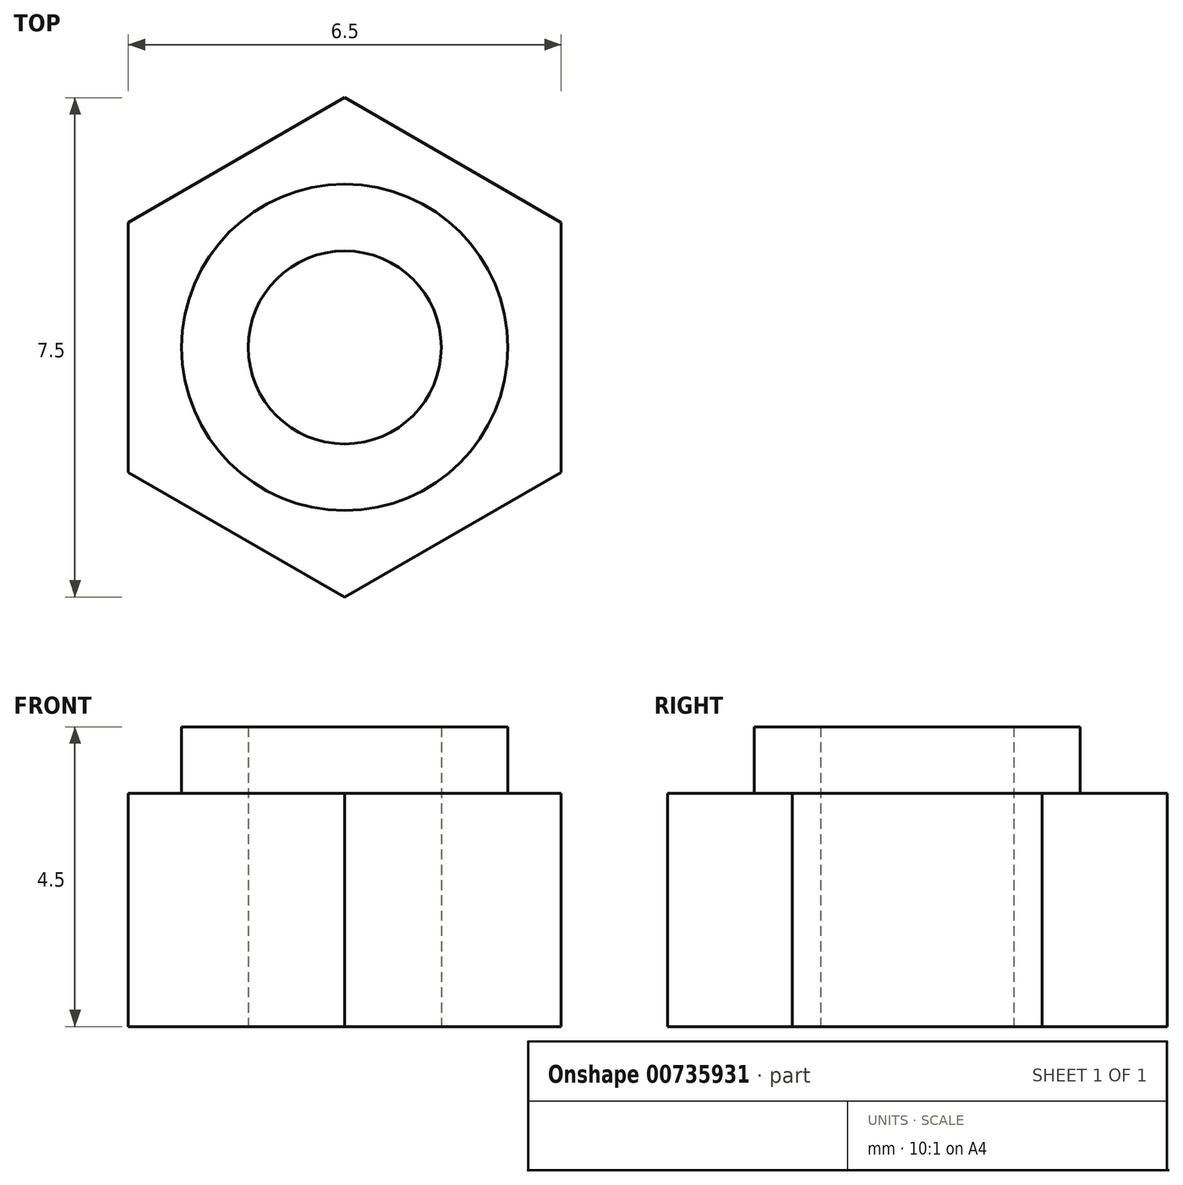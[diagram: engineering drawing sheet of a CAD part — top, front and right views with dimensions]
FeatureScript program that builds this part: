
annotation { "Feature Type Name" : "Feature", "Feature Type Description" : "" }
export const myFeature = defineFeature(function(context is Context, id is Id, definition is map)
    precondition{}
    {
        {
            var Q0;
            Q0=qCreatedBy(makeId("Top.planeOp"),FACE);
            var sketch = newSketch(context, id + "F0", { "sketchPlane" : qUnion([Q0])});
            skCircle(sketch, "E0", {"center": v(0, 0) * mm, "radius": 1.45 * mm});
            skCircle(sketch, "E1", {"center": v(0, 0) * mm, "radius": 2.45 * mm});
            skLineSegment(sketch, "E2.0", {"start": v(3.25, 1.88) * mm, "end": v(3.25, -1.88) * mm});
            skLineSegment(sketch, "E2.1", {"start": v(3.25, -1.88) * mm, "end": v(0, -3.75) * mm});
            skLineSegment(sketch, "E2.2", {"start": v(0, -3.75) * mm, "end": v(-3.25, -1.88) * mm});
            skLineSegment(sketch, "E2.3", {"start": v(-3.25, -1.88) * mm, "end": v(-3.25, 1.88) * mm});
            skLineSegment(sketch, "E2.4", {"start": v(-3.25, 1.88) * mm, "end": v(0, 3.75) * mm});
            skLineSegment(sketch, "E2.5", {"start": v(0, 3.75) * mm, "end": v(3.25, 1.88) * mm});
            skPoint(sketch, "E2.0.midPoint", {"position": v(3.25, 0) * mm});
            skSolve(sketch);
        }
        {
            var Q0;
            Q0=makeQuery(id+"F0.imprint","IMPRINT",FACE,{"disambiguationData":[TD([[makeQuery(id+"F0.imprint","IMPRINT",EDGE,{"derivedFrom":sQuery(id+"F0.wireOp",EDGE,"E0")}),-1.0]])]});
            extrude(context, id + "F1", {"entities" : qUnion([Q0]), "depth" : 2.5 * mm, "offsetDistance" : 25 * mm});
        }
        {
            var Q0;
            Q0=makeQuery(id+"F1.opExtrude","CAP_FACE",FACE,{"disambiguationData":[OSD([sQuery(id+"F0.wireOp",EDGE,"E0"),sQuery(id+"F0.wireOp",EDGE,"E1")])],"isStart":false});
            var Q1;
            Q1=makeQuery(id+"FWVlSdrg7Ynwrlk_1.opExtrude","CAP_FACE",FACE,{"disambiguationData":[OSD([sQuery(id+"F0.wireOp",EDGE,"RvXAe5nJ-QZyL-t199-jAbp-rAlAif7aGyIv"),sQuery(id+"F0.wireOp",EDGE,"E1")])],"isStart":false});
            extrude(context, id + "F2", {"entities" : qUnion([Q0, Q1]), "operationType" : NewBodyOperationType.ADD, "depth" : 2 * mm, "offsetDistance" : 25 * mm});
        }
        {
            var Q0;
            Q0=makeQuery(id+"F0.imprint","IMPRINT",FACE,{"disambiguationData":[TD([[makeQuery(id+"F0.imprint","IMPRINT",EDGE,{"derivedFrom":sQuery(id+"F0.wireOp",EDGE,"E1")}),-1.0]])]});
            extrude(context, id + "F3", {"entities" : qUnion([Q0]), "operationType" : NewBodyOperationType.ADD, "depth" : 3.5 * mm, "offsetDistance" : 25 * mm});
        }
    });
